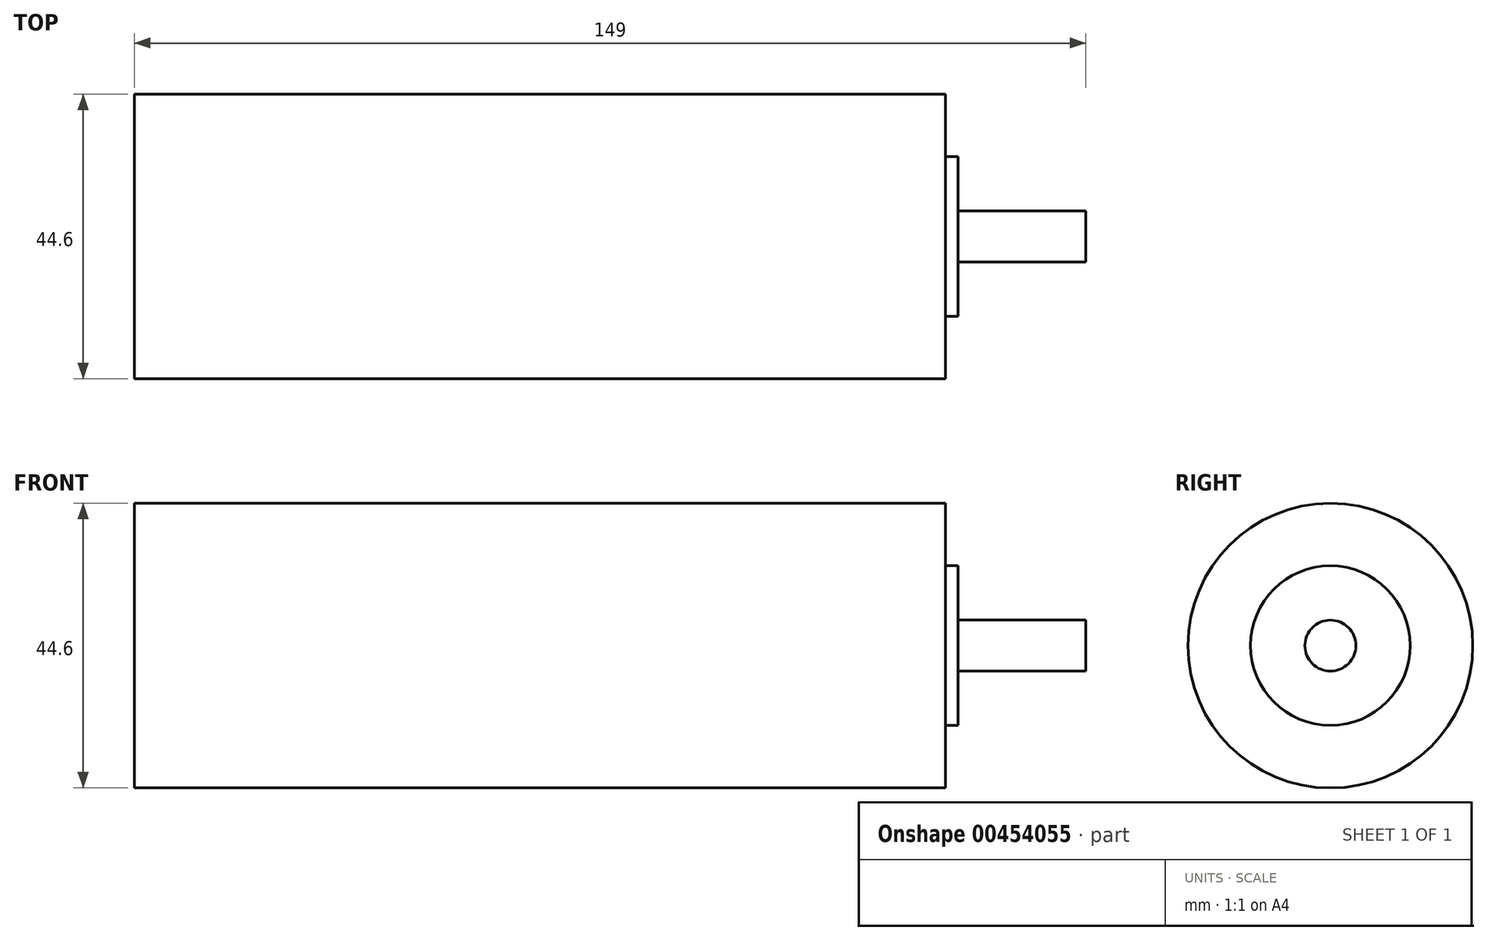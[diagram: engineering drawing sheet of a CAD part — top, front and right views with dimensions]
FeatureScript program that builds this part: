
annotation { "Feature Type Name" : "Feature", "Feature Type Description" : "" }
export const myFeature = defineFeature(function(context is Context, id is Id, definition is map)
    precondition{}
    {
        {
            var Q0;
            Q0=qCreatedBy(makeId("Right.planeOp"),FACE);
            var sketch = newSketch(context, id + "F0", { "sketchPlane" : qUnion([Q0])});
            skCircle(sketch, "E0", {"center": v(0, 0) * mm, "radius": 22.3 * mm});
            skSolve(sketch);
        }
        {
            var Q0;
            Q0 = qSketchRegion(id + "F0", true);
            extrude(context, id + "F1", {"entities" : qUnion([Q0]), "depth" : 127 * mm, "offsetDistance" : 25 * mm});
        }
        {
            var Q0;
            Q0=makeQuery(id+"F1.opExtrude","CAP_FACE",FACE,{"disambiguationData":[OSD([sQuery(id+"F0.wireOp",EDGE,"E0")])],"isStart":false});
            var sketch = newSketch(context, id + "F2", { "sketchPlane" : qUnion([Q0])});
            skCircle(sketch, "E1", {"center": v(0, 0) * mm, "radius": 12.5 * mm});
            skSolve(sketch);
        }
        {
            var Q0;
            Q0 = qSketchRegion(id + "F2", true);
            extrude(context, id + "F3", {"entities" : qUnion([Q0]), "operationType" : NewBodyOperationType.ADD, "depth" : 2 * mm, "offsetDistance" : 25 * mm});
        }
        {
            var Q0;
            Q0=makeQuery(id+"F3.opExtrude","CAP_FACE",FACE,{"disambiguationData":[OSD([sQuery(id+"F2.wireOp",EDGE,"E1")])],"isStart":false});
            var sketch = newSketch(context, id + "F4", { "sketchPlane" : qUnion([Q0])});
            skCircle(sketch, "E2", {"center": v(0, 0) * mm, "radius": 4 * mm});
            skSolve(sketch);
        }
        {
            var Q0;
            Q0 = qSketchRegion(id + "F4", true);
            extrude(context, id + "F5", {"entities" : qUnion([Q0]), "operationType" : NewBodyOperationType.ADD, "depth" : 20 * mm, "offsetDistance" : 25 * mm});
        }
    });
